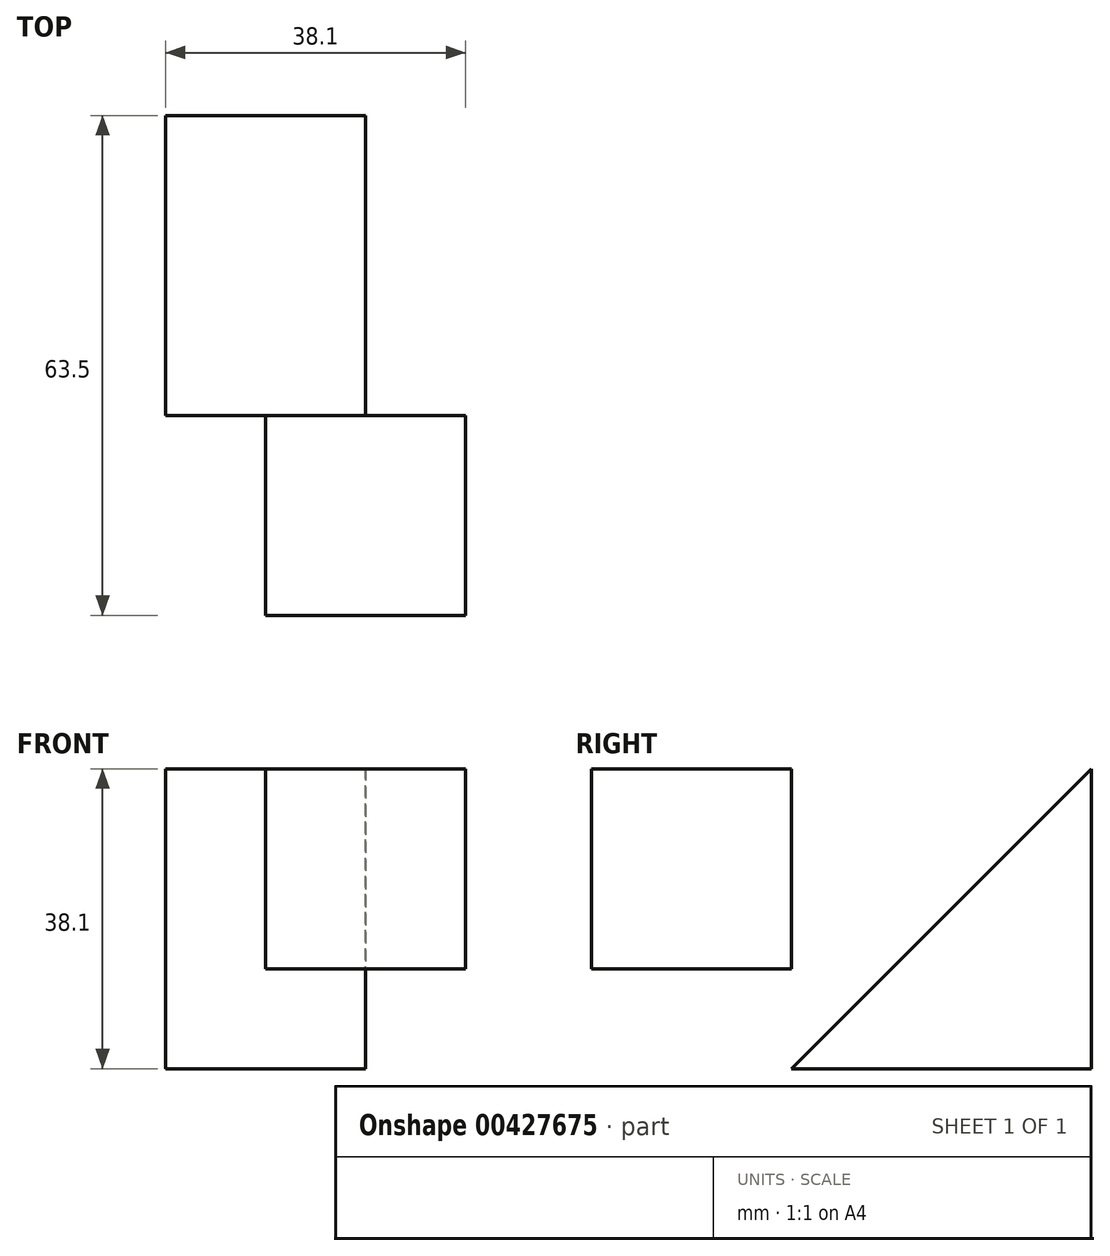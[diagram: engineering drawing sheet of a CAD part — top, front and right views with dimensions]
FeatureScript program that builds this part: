
annotation { "Feature Type Name" : "Feature", "Feature Type Description" : "" }
export const myFeature = defineFeature(function(context is Context, id is Id, definition is map)
    precondition{}
    {
        {
            var Q0;
            Q0=qCreatedBy(makeId("Front.planeOp"),FACE);
            var sketch = newSketch(context, id + "F0", { "sketchPlane" : qUnion([Q0])});
            skLineSegment(sketch, "E0", {"start": v(0, 0) * mm, "end": v(0, 38.1) * mm});
            skLineSegment(sketch, "E1", {"start": v(0, 38.1) * mm, "end": v(12.7, 38.1) * mm});
            skLineSegment(sketch, "E2", {"start": v(12.7, 38.1) * mm, "end": v(12.7, 12.7) * mm});
            skLineSegment(sketch, "E3", {"start": v(12.7, 12.7) * mm, "end": v(38.1, 12.7) * mm});
            skLineSegment(sketch, "E4", {"start": v(38.1, 12.7) * mm, "end": v(38.1, 38.1) * mm});
            skLineSegment(sketch, "E5", {"start": v(38.1, 38.1) * mm, "end": v(12.7, 38.1) * mm});
            skLineSegment(sketch, "E6", {"start": v(38.1, 12.7) * mm, "end": v(38.1, 0) * mm});
            skLineSegment(sketch, "E7", {"start": v(38.16, -0.2) * mm, "end": v(0, 0) * mm});
            skSolve(sketch);
        }
        {
            var Q0;
            Q0=qCreatedBy(makeId("Right.planeOp"),FACE);
            var sketch = newSketch(context, id + "F1", { "sketchPlane" : qUnion([Q0])});
            skLineSegment(sketch, "E8", {"start": v(0, 0) * mm, "end": v(38.1, 0) * mm});
            skLineSegment(sketch, "E9", {"start": v(38.1, 0) * mm, "end": v(38.1, 38.1) * mm});
            skLineSegment(sketch, "E10", {"start": v(38.1, 38.1) * mm, "end": v(0, 0) * mm});
            skSolve(sketch);
        }
        {
            var Q0;
            Q0 = qSketchRegion(id + "F1", true);
            extrude(context, id + "F2", {"entities" : qUnion([Q0]), "depth" : 25.4 * mm});
        }
        {
            var Q0;
            Q0 = qSketchRegion(id + "F0", true);
            extrude(context, id + "F3", {"entities" : qUnion([Q0]), "depth" : 25.4 * mm});
        }
    });
